# Revit family: PH1400U
name_source: partatom
category: Generic Models
revit_build: Autodesk Revit Architecture 2012 (Build: 20110309_2315(x64)
units: mm (PartAtom-declared; Revit-internal decimal feet)

## types (1)
- PH1400U
    * = Lens does not ship with projector
    Accessories - N8000-8830 = NEC OPS PC with Intel Core i5, 320GB Hard Drive, Windows Embedded Standard 7
    Accessories - NP25FL = 0.67 : 1 fixed short throw lens
    Accessories - NP26ZL = 1.39 - 1.87 : 1 zoom lens
    Accessories - NP27ZL = 1.87 - 2.56 : 1 zoom lens
    Accessories - NP28ZL = 2.56 - 4.16 : 1 zoom lens
    Accessories - NP29ZL = 4.16 - 6.96 : 1 zoom lens
    Accessories - NP32ZL = 0.90 - 1.1 : 1 zoom lens
    Accessories - PHCase-01 = ATA-Certified case for shipping and secure storage
    Accessories - RGBCBL-PJPX = Replacement RGB signal cable
    Accessories - RMT-PJ33 = Replacement Remote Control
    Accessories - SB-01HC = SD/HD-SDI input card
    Assembly Code = E1020500
    Description = Professional Installation Projector
    Dimensions (WxDxH) = 22.7 x 9.3 x 22 in. / 578 x 235 x 558 mm
    Environmental - Humidity = 20-80% non-condensing
    Environmental - Operating Temperature = 32deg - 104degF / 0deg - 40degC
    Environmental - Storage = -14deg - 122deg / -10deg - 60degC
    Fan Noise = 48 dB normal / 44 dB eco
    Input Current = 6.4A
    Installation Orientation = Floor/Front, Floor/Rear, Ceiling/Front, Ceiling/Rear
    Manufacturer = NEC
    Model = PH1400U
    Net Weight = 87.1 lb / 39.5 kg
    Optical - Contrast Ratio (up to) = 2000 : 1
    Optical - Display /Technology = 0.96in DMD
    Optical - Keystone Correction = +/- 35deg horizontal, +/- 30deg vertical
    Optical - Lamp Life (up to) = 2500 hours normal / 3000 hours eco
    Optical - Lamp Type = (2) 465W AC
    Optical - Lens* F-number, f-number NP25FL = F=2.5, f=14.6
    Optical - Lens* F-number, f-number NP26ZL = F=2.5, f=28.9 to 38.9mm
    Optical - Lens* F-number, f-number NP27ZL = F=2.5, f=39.0 to 53.4mm
    Optical - Lens* F-number, f-number NP28ZL = F=2.5, f=52.4 to 85.3mm
    Optical - Lens* F-number, f-number NP29ZL = F=2.5, f=84.9 to 142mm
    Optical - Lens* F-number, f-number NP32ZL = F=2.5, f=19.4 to 23.3mm
    Optical - Lens* Focus = Power
    Optical - Lens* Shift = Power: +55/-40% vertical, +/-20% horizontal
    Optical - Lens* Zoom = Power
    Optical - Light Output (lumens) = 14,000 center-screen lumens (13,500 ANSI lumens)
    Optical - Projection Angle = 2.7deg 11.2deg tele / 4.4 to 15.4deg wide
    Optical - Projection Distance = 1.8 to 243 ft / 0.55 to 74m
    Optical - Resolution Maximum = WUXGA 1920 x 1200
    Optical - Resolution Native = WUXGA 1920 x 1200
    Optical - Screen Size (diagonal) = 80 to 500 in. / 2 to 12.7m
    Optical - Throw Ratio NP25FL = 0.67 : 1
    Optical - Throw Ratio NP26FL = 1.39 - 1.87 : 1
    Optical - Throw Ratio NP27ZL = 1.87 - 2.56 : 1
    Optical - Throw Ratio NP28ZL = 2.56 - 4.16 : 1
    Optical - Throw Ratio NP29ZL = 4.16 - 6.96 : 1
    Optical - Throw Ratio NP32ZL = 0.9 - 1.1 : 1
    Optional Lenses = NP25FL, NP26ZL, NP27ZL, NP28ZL, NP29ZL
    Power Consumption (Normal/Eco Mode/Standby/Network Standby/Standby-Power Saving = 1215W / 985W / 90W / 0.5W
    Power Requirements = 200 - 240V AC
    Signal Compatibility/Connectivity - External Control = RS-232, IR, Wired LAN, DDC/CI, USB, Wireless LAN (optional)
    Signal Compatibility/Connectivity - Input/Output Terminals 1 Stereo = DVI-D (Dual Link)
    Signal Compatibility/Connectivity - Input/Output Terminals Monitor Out = VGA 15-pin D-sub
    Signal Compatibility/Connectivity - Input/Output Terminals Option Slot = HD/SD-SDI
    Signal Compatibility/Connectivity - Input/Output Terminals RGB1 (analog) = VGA 15-pin D-sub
    Signal Compatibility/Connectivity - Input/Output Terminals RGB2 (analog) = VGA 15-pin D-sub
    Signal Compatibility/Connectivity - Input/Output Terminals RGB3 (analog) = 5-BNC
    Signal Compatibility/Connectivity - Input/Output Terminals RGB4 (digital) = HDMI w/ HDCP
    Signal Compatibility/Connectivity - Input/Output Terminals RGB5 (digital) = DisplayPort w/ HDCP
    Signal Compatibility/Connectivity - Input/Output Terminals Video 1 = RCA
    Signal Compatibility/Connectivity - Input/Output Terminals Video 2 = S-Video
    Signal Compatibility/Connectivity - Macintosh Compatibility = Yes
    Signal Compatibility/Connectivity - Networking = RJ-45 and Wireless LAN (optional)
    Signal Compatibility/Connectivity - PC Signal Compatibility = VGA, SVGA, XGA, SXGA, SXGA+, UXGA, WUXGA
    Signal Compatibility/Connectivity - SD/HD Video Signal Compatibility = 480i, 480p, 576i, 576p, 720p, 1080i, 1080p, 1080P120
    Signal Compatibility/Connectivity - Scan Rate, Horizontal = 15 - 108 kHz
    Signal Compatibility/Connectivity - Scan Rate, Vertical = 48 - 120 Hz
    Signal Compatibility/Connectivity - Supported Video Standards = NTSC, NTSC4.43, PAL, PAL-60, PAL-M, PAL-N, SECAM
    Signal Compatibility/Connectivity - Sync Compatibility = Separate Sync /Composite Sync / Sync on G
    Signal Compatibility/Connectivity - USB = Viewer
    URL = www.necdisplay.com
    Warranty - ADVEXON1-I = Extends term of InstaCare service program to 2 years
    Warranty - ADVEXON2-I = Extends term of InstaCare service program to 3 years
    Warranty - NECEW1-I = Extends term of parts and labor warranty to 4 years
    Warranty - NECEW2-I = Extends term of parts and labor warranty to 5 years
